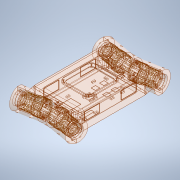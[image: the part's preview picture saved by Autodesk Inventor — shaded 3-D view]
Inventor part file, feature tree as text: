
AUTODESK INVENTOR PART (.ipt)
format: ipt  version: 2020.2 (Build 242310000, 310)  size: 20,582,912 bytes
history: native  units: mm
features: other x48, extrude x38, sketch x12, pattern_circular x8, plane x7, thicken_offset x7, chamfer x6, mirror x5, boolean_combine x5, revolve x3, sweep x2, fillet x2, split x2, loft x1
ambient origin geometry x8: Origin, YZ Plane, XZ Plane, XY Plane, X Axis, Y Axis, Z Axis, Center Point
bodies: Solid1 (feature_tree), body_up_Thicken106 (feature_tree), body_up_Thicken107 (feature_tree), body_up_Thicken108 (feature_tree), Solid14 (feature_tree)
feature tree (146):
  sketch  "Sketch1"  dims[d0=1.745329mm d1=1.0mm]
  sketch  "Sketch_3_division_plane"  dims[d49=67.2mm d50=0.0mm d53=0.0mm d54=0.0mm d55=90.0deg d60=67.2mm d61=0.0mm d63=10.0mm d65=47.2mm d66=0.0mm d67=38.0mm d68=10.0mm d69=23.0mm d77=4.1mm d78=3.3mm d79=90.0deg d80=7.0mm d81=28.0mm d97=3.490659mm d102=90.0deg d103=4.5mm d105=17.5mm d106=7.2mm d107=0.0mm d108=0.0mm d109=10.0mm d110=0.0mm d111=40.0mm d112=360.0deg d122=12.0mm d123=10.0mm d124=60.0deg d128=100.0mm d129=90.0mm d130=2.886751mm d143=56.2mm d144=48.0mm d146=4.0mm d147=2.5mm d148=3.1mm d149=5.0mm d150=8.0mm d151=0.0mm d152=6.0mm d153=0.0mm d154=57.7mm d155=0.0mm d156=57.7mm d157=0.0mm d161=6.0mm d162=67.2mm d163=45.2mm d164=0.0mm d165=0.0mm d166=90.0deg d167=10.0mm d168=0.0mm d173=20.0mm d174=360.0deg d179=0.0mm d180=0.0mm d183=20.0mm d184=360.0deg d186=20.0mm d187=360.0deg d190=214.629177mm d193=11.0mm d207=1.745329mm d208=100.0mm d209=0.0mm d210=90.0deg d211=5.0mm d212=3.1mm d213=2.5mm d215=0.0mm d216=8.0mm d217=0.0mm d218=52.504mm d219=0.0mm d220=6.0mm d221=0.0mm d222=52.504mm d223=0.0mm d224=45.2mm d225=29.5mm d226=1.6mm d227=6.981317mm d230=4.0mm d231=2.0mm d232=45.0deg d233=23.6mm d287=0.38mm d288=0.1mm d297=0.4mm d311=5.0mm d312=53.201mm d313=0.0mm d324=6.981317mm d325=0.8mm d326=2.8mm d328=7.0mm d329=6.0mm d338=20.0mm d340=10.0mm d341=10.0mm d343=10.0mm d345=4.0mm d346=52.354mm d347=0.0mm d348=80.0mm d349=360.0deg d352=2.5mm d353=1.0mm d355=6.981317mm d356=3.0mm d366=52.354mm d367=0.0mm d387=1.0mm d388=1.0mm d391=20.0mm d393=10.0mm d394=20.0mm d396=12.0mm d399=4.301042mm d400=5.4mm d401=6.981317mm d405=7.0mm d406=70.0mm d407=270.0deg d409=52.354mm d410=0.0mm d412=50.0mm d413=180.0deg d415=29.2mm d416=0.0mm d419=58.0mm d420=0.0mm d425=3.0mm d428=10.0mm d429=0.0mm d437=3.0mm d438=20.0mm d440=10.0mm d441=10.0mm d443=10.0mm d445=3.0mm d446=4.942038mm d449=10.0mm d451=10.0mm d452=10.0mm d453=5.65mm d456=10.0mm d460=5.0mm d464=40.0mm d468=12.6mm d469=23.783922mm d470=5.0mm d471=14.0mm d480=6.981317mm d481=2.0mm d482=20.0mm d483=6.0mm d484=2.0mm d485=8.726646mm d486=6.0mm d487=2.0mm d488=8.726646mm d489=20.0mm d491=12.5mm d492=10.0mm d494=10.0mm d496=7.5mm d504=4.5mm d505=8.0mm d506=1.745329mm d507=4.5mm d508=8.0mm d509=1.745329mm d510=20.0mm d511=360.0deg d513=27.690458mm d514=10.0mm d520=234.629177mm d524=8.0mm d525=6.0mm d528=10.0mm d529=0.0mm d533=67.2mm d534=2.4mm d535=2.0mm d536=45.0deg d538=160.0mm d539=4.5mm d540=0.12mm d541=0.04mm d542=2.8mm d543=0.6mm d546=5.0mm d550=50.0mm d551=0.0mm d552=2.0mm d553=0.0mm d554=2.0mm d555=0.0mm d624=171.639mm d625=0.0mm d638=0.405mm d639=0.405mm d642=1.605mm d643=1.605mm d644=1.605mm d645=1.605mm d646=1.605mm d647=1.605mm d648=1.605mm d649=1.605mm d650=1.605mm d651=1.605mm d652=1.605mm d653=1.605mm d654=1.605mm d655=1.605mm d656=1.605mm d657=1.605mm d658=1.605mm d659=1.605mm d660=1.605mm d661=1.605mm d662=1.605mm d663=1.605mm d664=1.605mm d665=1.605mm d680=1.0mm d710=103.0mm d711=18.0mm d712=361.950606mm d727=8.0mm d728=8.0mm d729=7.6mm d730=2.0mm d731=22.0mm d732=12.0mm d733=6.0mm d734=5.5mm d735=10.0mm d736=0.0mm d737=7.4mm d738=1.5mm d739=0.0mm d740=0.9mm d741=0.0mm d742=0.815mm d743=0.0mm d744=1.0mm d745=0.0mm d746=15.0mm d747=0.0mm d748=90.0deg d749=0.0mm d750=90.0deg d777=56.0mm d778=76.0mm d779=25.0mm d785=15.0mm d786=15.0mm d796=45.0deg d797=4.5mm d798=2.5mm d799=14.5mm d841=5.0mm d842=14.5mm d843=10.0mm d844=10.0mm d845=10.0mm d846=10.0mm d847=10.0mm d849=92.0mm d850=59.0mm d851=5.0mm d852=10.0mm d853=5.0mm d854=10.0mm d855=5.0mm d856=10.0mm d857=5.0mm d858=10.0mm d859=5.0mm d860=10.0mm d861=5.0mm d862=10.0mm d863=5.0mm d864=35.0mm d865=40.0mm d866=35.0mm d867=4.0mm d868=0.0mm d869=1.0mm d870=0.0mm d871=15.0mm d872=10.0mm d879=50.5mm d880=27.0mm d881=1.0mm d882=18.0mm d892=0.5mm d893=0.0mm d906=26.0mm d908=18.0mm d909=5.0mm d911=10.0mm d913=10.0mm d917=4.0mm d918=0.0mm d929=20.0mm d930=12.0mm d931=2.0mm d932=0.0mm d936=4.0mm d937=55.0mm d938=8.0mm d941=191.20124mm d942=0.405mm d943=0.405mm d944=0.6075mm d945=0.405mm d946=0.405mm d947=0.405mm d948=0.6075mm d949=0.405mm d952=20.0mm d953=0.4455mm d954=0.4455mm d955=0.4455mm d956=0.4455mm d957=0.4455mm d958=0.4455mm d959=0.4455mm d960=0.4455mm d969=0.81mm d970=0.81mm d971=0.405mm d972=0.81mm d973=0.81mm d974=0.6075mm d975=2.025mm d976=1.62mm d977=2.025mm d978=1.62mm d32=0.5mm d33=0.872665mm d34=0.5mm d35=0.872665mm d472=0.872665mm d720=0.5mm d721=0.872665mm d722=0.5mm d723=0.872665mm d899=0.5mm d900=0.872665mm d901=0.5mm d902=0.872665mm]
  plane  "Work Plane5"
  plane  "Work Plane4"
  plane  "Work Plane7"
  sketch  "Sketch2"  dims[d3=8.726646mm d4=3.0mm]
  sketch  "Sketch3"  dims[d5=37.0mm d6=2.0mm]
  sketch  "Sketch6"  dims[d10=42.0mm d11=6.5mm]
  sketch  "Sketch11"  dims[d14=3.0mm d15=42.0mm]
  revolve  "Revolution4"  [1 undecoded]
  extrude  "Extrusion4"  Depth=3.0mm
  revolve  "Revolution5"  [1 undecoded]
  extrude  "Extrusion19"  Depth=1.6mm
  extrude  "Extrusion37_CUT"  Depth=6.5mm
  sweep  "Sweep5"
  extrude  "Extrusion6-body begin"  Depth=3.0mm
  extrude  "Extrusion43"  Depth=260.0mm
  chamfer  "Chamfer12"  [1 undecoded]
  mirror  "Mirror9"
  boolean_combine  "Combine7"
  extrude  "Extrusion7"  TaperAngle=0.0deg  [1 undecoded]
  boolean_combine  "Combine3"
  other  "Thicken7_sof_hard_meshing"
  fillet  "Fillet7"  [1 undecoded]
  revolve  "Revolution6"  [1 undecoded]
  extrude  "Extrusion20"  TaperAngle=0.0deg  [1 undecoded]
  extrude  "Extrusion32"  Depth=10.0mm
  extrude  "Extrusion41"  Depth=12.0mm TaperAngle=0.0deg
  fillet  "Fillet8"  Radius=38.0mm
  extrude  "Extrusion34"  Depth=10.0mm
  pattern_circular  "Circular Pattern6"  [2 undecoded]
  extrude  "Extrusion35"  Depth=12.0mm
  pattern_circular  "Circular Pattern9"  [2 undecoded]
  extrude  "Extrusion36"  TaperAngle=90.0deg  [1 undecoded]
  pattern_circular  "Circular Pattern10"  [2 undecoded]
  extrude  "Extrusion39"  Depth=12.0mm
  chamfer  "Chamfer9"  Distance=3.490659mm
  chamfer  "Chamfer10"  Distance=4.5mm Angle=90.0deg
  sketch  "Sketch5"  dims[d7=1.6mm d9=1.6mm]
  extrude  "Extrusion10"  Depth=12.0mm
  extrude  "Extrusion11"  Depth=12.0mm
  pattern_circular  "Circular Pattern1"  [2 undecoded]
  plane  "Work Plane6"
  extrude  "Extrusion15"  Depth=10.0mm TaperAngle=0.0deg
  extrude  "Extrusion18"  Depth=12.0mm TaperAngle=360.0deg
  extrude  "Extrusion16"  Depth=12.0mm
  extrude  "Extrusion17"  Depth=10.0mm
  extrude  "Extrusion22"  TaperAngle=60.0deg  [1 undecoded]
  extrude  "Extrusion23"  Depth=12.0mm
  extrude  "Extrusion24"  Depth=12.0mm
  extrude  "Extrusion25"  Depth=12.0mm
  mirror  "Mirror5"
  other  "Thicken1_to compensate material shrinkage"
  split  "Split6"
  chamfer  "Chamfer7"  Distance=56.2mm
  chamfer  "Chamfer8"  Distance=48.0mm
  sketch  "Sketch10"  dims[d12=7.0mm d13=27.0mm]
  chamfer  "Chamfer3"  Distance=4.0mm
  extrude  "Extrusion47"  Depth=12.0mm
  other  "motor_front_out_thicken"
  other  "insert_thicken_1"
  other  "screw_thicken_1"
  other  "screw_thicken_2"
  other  "insert_thicken_2"
  other  "insert_thicken_3"
  other  "screw_thicken_3"
  other  "screw_thicken_4"
  other  "insert_thicken_4"
  other  "screw_thicken_5"
  other  "insert_thicken_5"
  other  "insert_thicken_6"
  other  "screw_thicken_6"
  thicken_offset  "Thicken113"
  thicken_offset  "Thicken117"
  thicken_offset  "Thicken114"
  thicken_offset  "Thicken115"
  thicken_offset  "Thicken116"
  boolean_combine  "Combine9"
  boolean_combine  "Combine10"
  pattern_circular  "Circular Pattern2"  [2 undecoded]
  plane  "Work Plane12"
  sketch  "Sketch19"  dims[d16=8.0mm d17=260.0mm]
  plane  "Work Plane13"
  extrude  "Extrusion50"  Depth=5.0mm
  extrude  "Extrusion51"  Depth=12.0mm TaperAngle=0.0deg
  extrude  "Extrusion52"  Depth=12.0mm TaperAngle=0.0deg
  extrude  "Extrusion53"  Depth=12.0mm TaperAngle=0.0deg
  extrude  "Extrusion54"  Depth=12.0mm TaperAngle=0.0deg
  loft  "Loft3"
  thicken_offset  "Thicken101"
  pattern_circular  "Circular Pattern11"  [2 undecoded]
  extrude  "Extrusion44"  Depth=12.0mm
  extrude  "Extrusion45"  TaperAngle=0.0deg  [1 undecoded]
  extrude  "Extrusion46"  TaperAngle=90.0deg  [1 undecoded]
  mirror  "Mirror10_screw"
  split  "Split8"
  other  "thicken_cover"
  boolean_combine  "Combine14"
  other  "thicken_main_body_up"
  pattern_circular  "Circular Pattern4"  [2 undecoded]
  pattern_circular  "Circular Pattern5"  Count=2 Angle=360.0deg
  plane  "Work Plane8"
  other  "Split9_END"
  other  "main_body_up_thicken_2"
  sketch  "Sketch33"  dims[d27=35.453079mm]
  extrude  "Extrusion60"  TaperAngle=0.0deg  [1 undecoded]
  extrude  "Extrusion61"  Depth=12.0mm TaperAngle=360.0deg
  sketch  "Sketch34"  dims[d48=90.0deg]
  extrude  "Extrusion63"  Depth=12.0mm TaperAngle=360.0deg
  extrude  "Extrusion65"  Depth=12.0mm
  extrude  "Extrusion66"  Depth=12.0mm
  mirror  "Mirror14"
  mirror  "Mirror15"
  thicken_offset  "Thicken105"
  other  "motor_cover_1"
  other  "Srf5"
  other  "Pattern of main_body_up_thicken_1:19"
  other  "motor_mount_back_in"
  other  "Pattern of main_body_up_thicken_1:20"
  other  "motor_mount_back_out"
  other  "Srf6"
  other  "Pattern of motor_mount_thicken_front_out:23"
  other  "motor_cover_2"
  other  "Pattern of main_body_up_thicken_1:24"
  other  "motor_cover_3"
  other  "Pattern of main_body_up_thicken_1:25"
  other  "motor_cover_4"
  other  "motor_mount_thicken_front_in"
  other  "motor_mount_thicken_front_out"
  other  "Pattern of main_body_up_thicken_1:26"
  other  "motor_mount_thicken_back_in"
  other  "Pattern of main_body_up_thicken_1:28"
  other  "motor_mount_thicken_back_out"
  sketch  "Sketch27"  dims[d24=67.2mm]
  other  "Edges4"
  other  "main_body_up_thicken_1"
  other  "cover_thicken_1"
  other  "main_body_down_thicken"
  extrude  "ExtrusionSrf4"  Depth=12.0mm
  sweep  "SweepSrf2"
  other  "motor_mount_front_in"
  other  "motor_mount_front_out"
  other  "main_body"
  other  "cover"
  other  "main_body_up"
  other  "main_body_down"
note: 26 required parameter values undecoded (feature->parameter linkage not recoverable at this tier; creation-order binding heuristic only, values carry confidence <= 0.55)